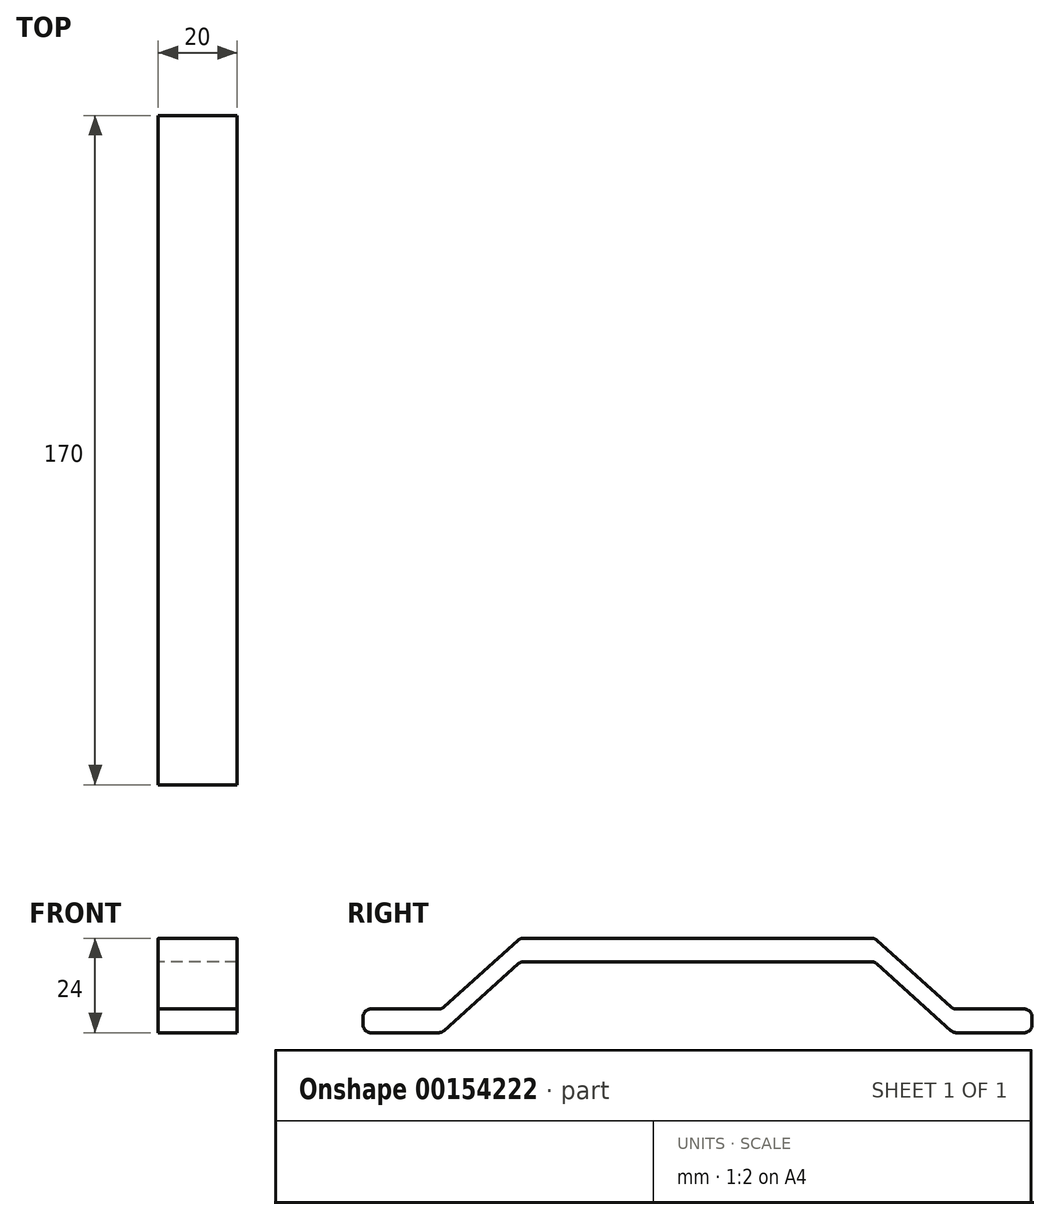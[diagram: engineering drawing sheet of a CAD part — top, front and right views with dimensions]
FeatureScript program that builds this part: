
annotation { "Feature Type Name" : "Feature", "Feature Type Description" : "" }
export const myFeature = defineFeature(function(context is Context, id is Id, definition is map)
    precondition{}
    {
        {
            var Q0;
            Q0=qCreatedBy(makeId("Right.planeOp"),FACE);
            var sketch = newSketch(context, id + "F0", { "sketchPlane" : qUnion([Q0])});
            skLineSegment(sketch, "E0", {"start": v(-83, 6) * mm, "end": v(-65.77, 6) * mm});
            skLineSegment(sketch, "E1", {"start": v(-44.23, 24) * mm, "end": v(0, 24) * mm});
            skLineSegment(sketch, "E2", {"start": v(0, 24) * mm, "end": v(0, 18) * mm, "construction": true});
            skLineSegment(sketch, "E3", {"start": v(0, 18) * mm, "end": v(-44.23, 18) * mm});
            skLineSegment(sketch, "E4", {"start": v(-45.57, 17.49) * mm, "end": v(-64.43, 0.51) * mm});
            skLineSegment(sketch, "E5", {"start": v(-65.77, 0) * mm, "end": v(-83, 0) * mm});
            skLineSegment(sketch, "E6", {"start": v(-85, 2) * mm, "end": v(-85, 4) * mm});
            skLineSegment(sketch, "E7", {"start": v(-65, 6) * mm, "end": v(-65, 0) * mm, "construction": true});
            skLineSegment(sketch, "E8", {"start": v(-45, 24) * mm, "end": v(-45, 18) * mm, "construction": true});
            skLineSegment(sketch, "E9", {"start": v(-75, 6) * mm, "end": v(-75, 0) * mm, "construction": true});
            skLineSegment(sketch, "E10", {"start": v(-45.57, 23.49) * mm, "end": v(-64.43, 6.51) * mm});
            skLineSegment(sketch, "E11.MirrorCS", {"start": v(75, 6) * mm, "end": v(75, 0) * mm, "construction": true});
            skLineSegment(sketch, "E12.MirrorCS", {"start": v(45, 24) * mm, "end": v(45, 18) * mm, "construction": true});
            skLineSegment(sketch, "E13.MirrorCS", {"start": v(65, 6) * mm, "end": v(65, 0) * mm, "construction": true});
            skLineSegment(sketch, "E14.MirrorCS", {"start": v(85, 2) * mm, "end": v(85, 4) * mm});
            skLineSegment(sketch, "E15.MirrorCS", {"start": v(65.77, 0) * mm, "end": v(83, 0) * mm});
            skLineSegment(sketch, "E16.MirrorCS", {"start": v(45.57, 17.49) * mm, "end": v(64.43, 0.51) * mm});
            skLineSegment(sketch, "E17.MirrorCS", {"start": v(45.57, 23.49) * mm, "end": v(64.43, 6.51) * mm});
            skLineSegment(sketch, "E18.MirrorCS", {"start": v(83, 6) * mm, "end": v(65.77, 6) * mm});
            skLineSegment(sketch, "E19.MirrorCS", {"start": v(44.23, 24) * mm, "end": v(0, 24) * mm});
            skLineSegment(sketch, "E20.MirrorCS", {"start": v(0, 18) * mm, "end": v(44.23, 18) * mm});
            skLineSegment(sketch, "E21.MirrorCS", {"start": v(0, 24) * mm, "end": v(0, 18) * mm});
            skPoint(sketch, "E22.visualSharp", {"position": v(-85, 0) * mm});
            skArc(sketch, "E22.filletArc", {"start": v(-85, 2) * mm, "mid": v(-84.41, 0.59) * mm, "end": v(-83, 0) * mm});
            skPoint(sketch, "E23.visualSharp", {"position": v(-85, 6) * mm});
            skArc(sketch, "E23.filletArc", {"start": v(-83, 6) * mm, "mid": v(-84.41, 5.41) * mm, "end": v(-85, 4) * mm});
            skPoint(sketch, "E24.visualSharp", {"position": v(-65, 0) * mm});
            skArc(sketch, "E24.filletArc", {"start": v(-65.77, 0) * mm, "mid": v(-65.05, 0.13) * mm, "end": v(-64.43, 0.51) * mm});
            skPoint(sketch, "E25.visualSharp", {"position": v(-65, 6) * mm});
            skArc(sketch, "E25.filletArc", {"start": v(-65.77, 6) * mm, "mid": v(-65.05, 6.13) * mm, "end": v(-64.43, 6.51) * mm});
            skPoint(sketch, "E26.visualSharp", {"position": v(-45, 24) * mm});
            skArc(sketch, "E26.filletArc", {"start": v(-44.23, 24) * mm, "mid": v(-44.95, 23.87) * mm, "end": v(-45.57, 23.49) * mm});
            skPoint(sketch, "E27.visualSharp", {"position": v(-45, 18) * mm});
            skArc(sketch, "E27.filletArc", {"start": v(-44.23, 18) * mm, "mid": v(-44.95, 17.87) * mm, "end": v(-45.57, 17.49) * mm});
            skPoint(sketch, "E28.visualSharp", {"position": v(45, 24) * mm});
            skArc(sketch, "E28.filletArc", {"start": v(45.57, 23.49) * mm, "mid": v(44.95, 23.87) * mm, "end": v(44.23, 24) * mm});
            skPoint(sketch, "E29.visualSharp", {"position": v(45, 18) * mm});
            skArc(sketch, "E29.filletArc", {"start": v(45.57, 17.49) * mm, "mid": v(44.95, 17.87) * mm, "end": v(44.23, 18) * mm});
            skPoint(sketch, "E30.visualSharp", {"position": v(65, 0) * mm});
            skArc(sketch, "E30.filletArc", {"start": v(64.43, 0.51) * mm, "mid": v(65.05, 0.13) * mm, "end": v(65.77, 0) * mm});
            skPoint(sketch, "E31.visualSharp", {"position": v(85, 0) * mm});
            skArc(sketch, "E31.filletArc", {"start": v(83, 0) * mm, "mid": v(84.41, 0.59) * mm, "end": v(85, 2) * mm});
            skPoint(sketch, "E32.visualSharp", {"position": v(85, 6) * mm});
            skArc(sketch, "E32.filletArc", {"start": v(85, 4) * mm, "mid": v(84.41, 5.41) * mm, "end": v(83, 6) * mm});
            skPoint(sketch, "E33.visualSharp", {"position": v(65, 6) * mm});
            skArc(sketch, "E33.filletArc", {"start": v(64.43, 6.51) * mm, "mid": v(65.05, 6.13) * mm, "end": v(65.77, 6) * mm});
            skSolve(sketch);
        }
        {
            var Q0;
            Q0 = qSketchRegion(id + "F0", true);
            extrude(context, id + "F1", {"entities" : qUnion([Q0]), "depth" : 20 * mm});
        }
    });
